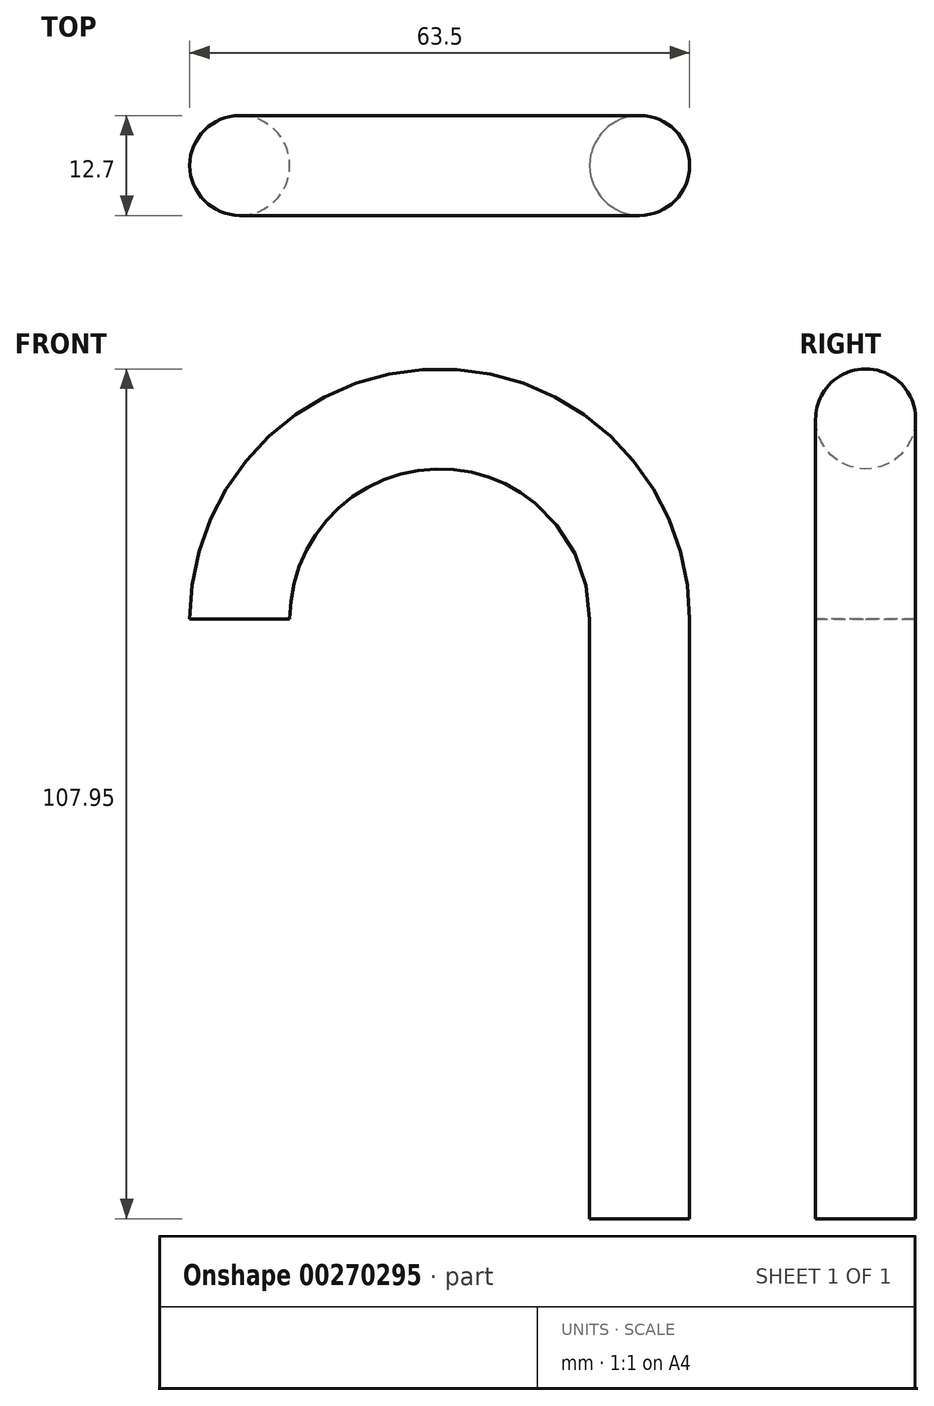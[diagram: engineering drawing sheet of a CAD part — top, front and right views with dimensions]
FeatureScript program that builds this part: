
annotation { "Feature Type Name" : "Feature", "Feature Type Description" : "" }
export const myFeature = defineFeature(function(context is Context, id is Id, definition is map)
    precondition{}
    {
        {
            var Q0;
            Q0=qCreatedBy(makeId("Front.planeOp"),FACE);
            var sketch = newSketch(context, id + "F0", { "sketchPlane" : qUnion([Q0])});
            skLineSegment(sketch, "E0", {"start": v(0, 0) * mm, "end": v(0, 76.2) * mm});
            skArc(sketch, "E1", {"start": v(0, 76.2) * mm, "mid": v(-25.4, 101.6) * mm, "end": v(-50.8, 76.2) * mm});
            skSolve(sketch);
        }
        {
            var Q0;
            Q0=qCreatedBy(makeId("Top.planeOp"),FACE);
            var sketch = newSketch(context, id + "F1", { "sketchPlane" : qUnion([Q0])});
            skCircle(sketch, "E2", {"center": v(0, 0) * mm, "radius": 6.35 * mm});
            skSolve(sketch);
        }
        {
            var Q0;
            Q0 = qSketchRegion(id + "F1", true);
            var Q1;
            Q1 = qConstructionFilter(qBodyType(qCreatedBy(id + "F0" ,EDGE), BodyType.WIRE), ConstructionObject.NO);
            sweep(context, id + "F2", {"profiles" : qUnion([Q0]), "path" : qUnion([Q1])});
        }
    });
